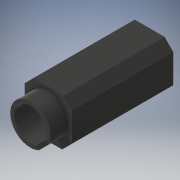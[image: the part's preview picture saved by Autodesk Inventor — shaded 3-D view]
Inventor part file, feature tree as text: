
AUTODESK INVENTOR PART (.ipt)
format: ipt  version: 2017 (Build 210142000, 142)  size: 157,184 bytes
history: native  units: in
note: dims shown in document units (in); Inventor stores cm internally (conversion verified against a paired STEP export)
features: extrude x5, sketch x5, fillet x1
ambient origin geometry x8: Origin, YZ Plane, XZ Plane, XY Plane, X Axis, Y Axis, Z Axis, Center Point
bodies: Body1 (feature_tree)
feature tree (11):
  extrude  "Extrusion7"  Depth=1.5551in
  extrude  "Extrusion8"  Depth=3.937in TaperAngle=0.0deg
  extrude  "Extrusion10"  Depth=3.937in TaperAngle=0.0deg
  extrude  "Extrusion11"  Depth=0.9843in TaperAngle=0.0deg
  extrude  "Extrusion12"  Depth=0.0787in TaperAngle=0.0deg
  fillet  "Fillet1"  Radius=0.4528in
  sketch  "Sketch1"  dims[d33=1.5551in d34=1.5551in]
  sketch  "Sketch8"  dims[d35=0.7874in d36=3.937in d37=0.0in]
  sketch  "Sketch10"  dims[d38=1.0827in d39=3.937in d40=0.0in]
  sketch  "Sketch11"  dims[d44=1.3386in d45=0.9843in d46=0.0in]
  sketch  "Sketch12"  dims[d47=1.3189in d48=0.5906in d49=0.0in d50=0.4528in d51=0.7874in d52=0.0in d53=0.0787in]
